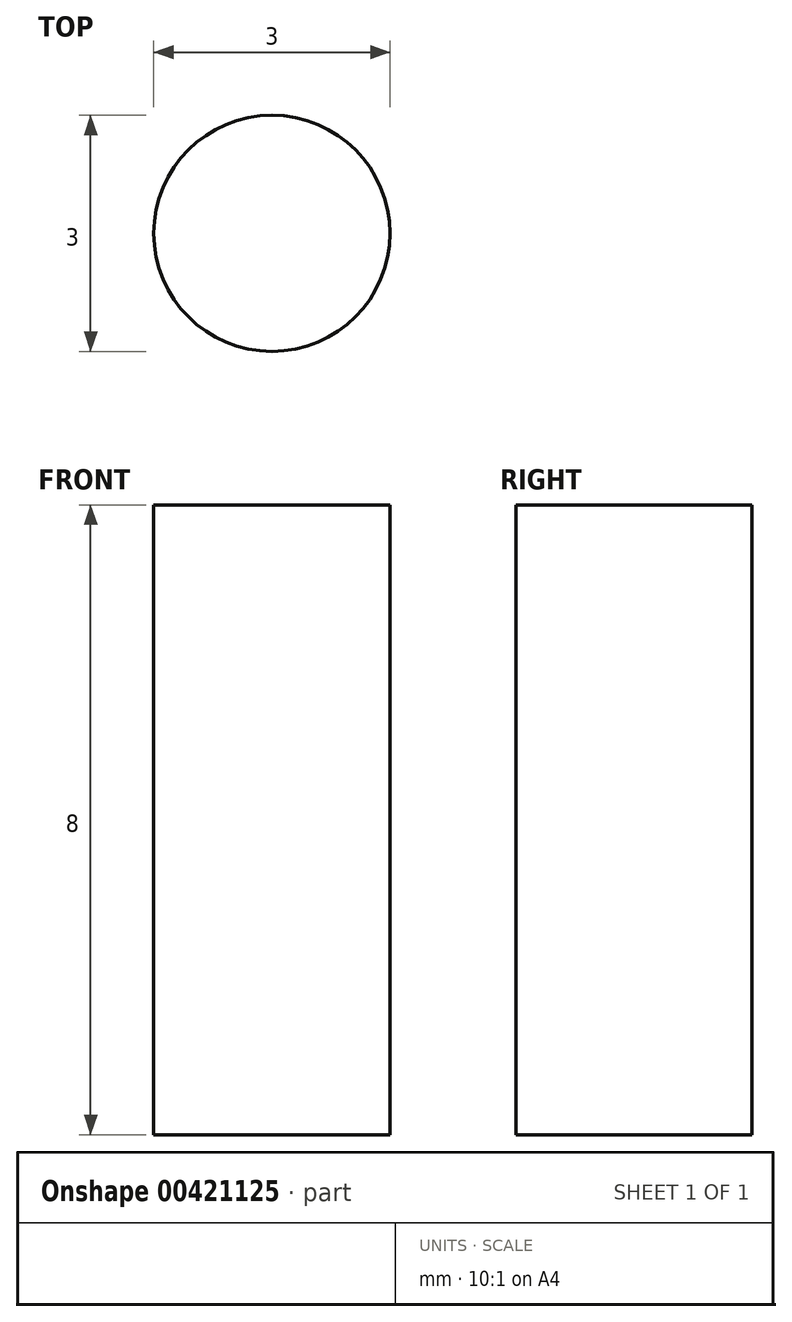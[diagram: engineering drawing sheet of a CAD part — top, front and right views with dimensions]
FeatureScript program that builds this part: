
annotation { "Feature Type Name" : "Feature", "Feature Type Description" : "" }
export const myFeature = defineFeature(function(context is Context, id is Id, definition is map)
    precondition{}
    {
        {
            var Q0;
            Q0=qCreatedBy(makeId("Top.planeOp"),FACE);
            var sketch = newSketch(context, id + "F0", { "sketchPlane" : qUnion([Q0])});
            skCircle(sketch, "E0", {"center": v(0, 0) * mm, "radius": 1.5 * mm});
            skSolve(sketch);
        }
        {
            var Q0;
            Q0=makeQuery(id+"F0.imprint","IMPRINT",FACE,{"disambiguationData":[TD([[makeQuery(id+"F0.imprint","IMPRINT",EDGE,{"derivedFrom":sQuery(id+"F0.wireOp",EDGE,"E0")}),1.0]])]});
            extrude(context, id + "F1", {"entities" : qUnion([Q0]), "depth" : 8 * mm});
        }
    });
